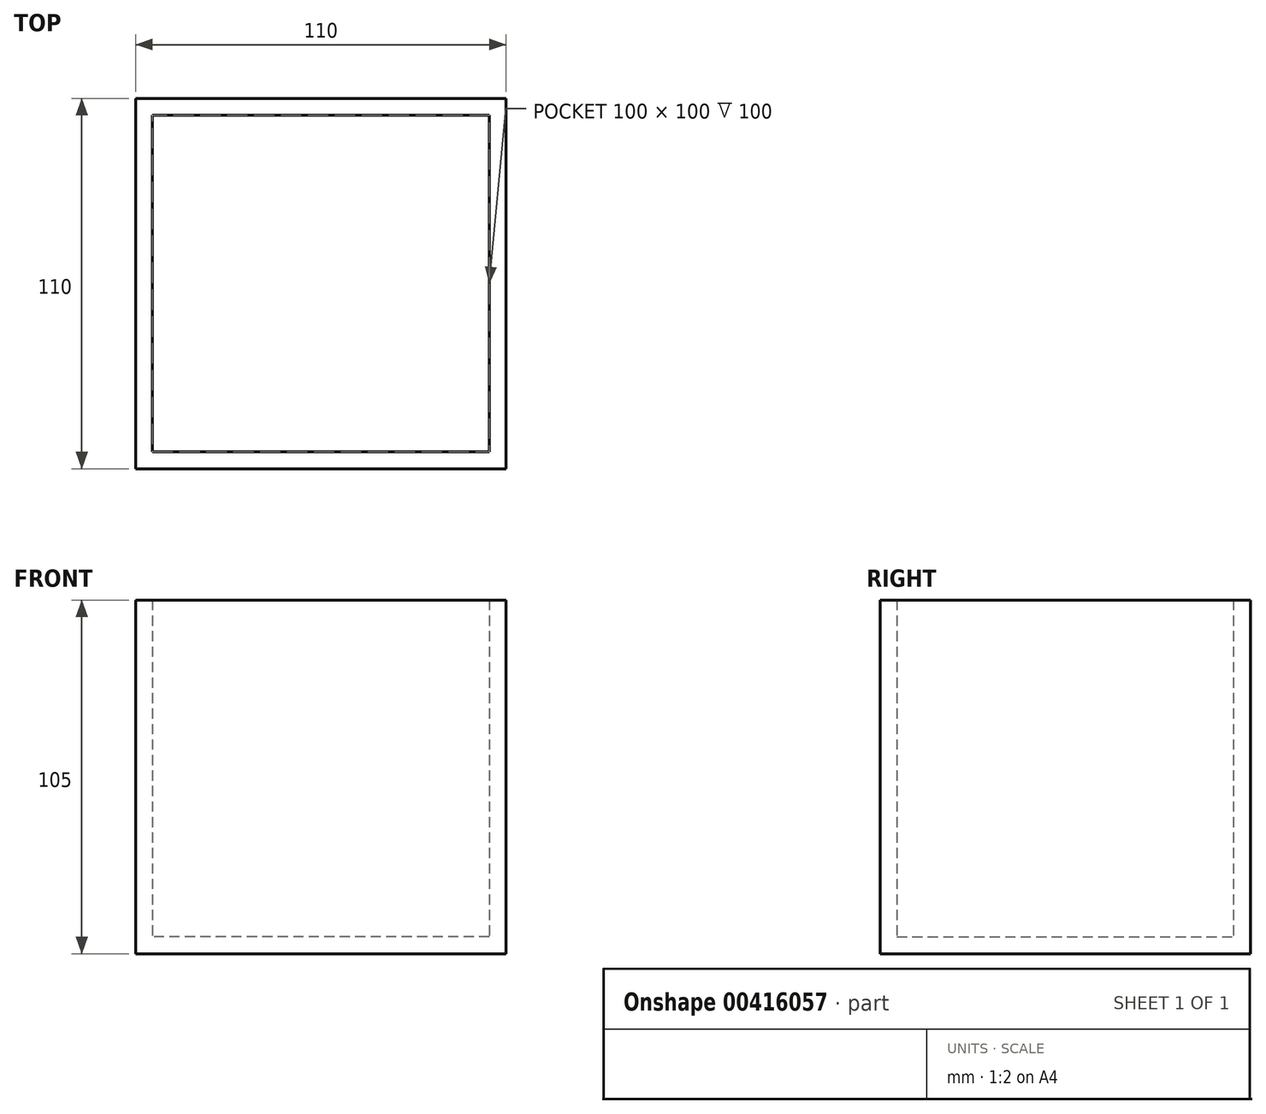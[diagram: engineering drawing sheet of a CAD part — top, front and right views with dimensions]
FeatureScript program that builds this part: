
annotation { "Feature Type Name" : "Feature", "Feature Type Description" : "" }
export const myFeature = defineFeature(function(context is Context, id is Id, definition is map)
    precondition{}
    {
        {
            var Q0;
            Q0=qCreatedBy(makeId("Top.planeOp"),FACE);
            var sketch = newSketch(context, id + "F0", { "sketchPlane" : qUnion([Q0])});
            skLineSegment(sketch, "E0.bottom", {"start": v(50, -50) * mm, "end": v(-50, -50) * mm});
            skLineSegment(sketch, "E0.top", {"start": v(50, 50) * mm, "end": v(-50, 50) * mm});
            skLineSegment(sketch, "E0.left", {"start": v(50, -50) * mm, "end": v(50, 50) * mm});
            skLineSegment(sketch, "E0.right", {"start": v(-50, -50) * mm, "end": v(-50, 50) * mm});
            skPoint(sketch, "E0.middle", {"position": v(0, 0) * mm});
            skSolve(sketch);
        }
        {
            var Q0;
            Q0=makeQuery(id+"F0.imprint","IMPRINT",FACE,{"disambiguationData":[TD([[makeQuery(id+"F0.imprint","IMPRINT",EDGE,{"derivedFrom":sQuery(id+"F0.wireOp",EDGE,"E0.bottom")}),-1.0]])]});
            extrude(context, id + "F1", {"entities" : qUnion([Q0]), "depth" : 100 * mm});
        }
        {
            var Q0;
            Q0=makeQuery(id+"F1.opExtrude","CAP_FACE",FACE,{"disambiguationData":[OSD([sQuery(id+"F0.wireOp",EDGE,"E0.bottom"),sQuery(id+"F0.wireOp",EDGE,"E0.top"),sQuery(id+"F0.wireOp",EDGE,"E0.left"),sQuery(id+"F0.wireOp",EDGE,"E0.right")])],"isStart":false});
            shell(context, id + "F2", {"entities" : qUnion([Q0]), "thickness" : 5 * mm, "oppositeDirection" : true});
        }
    });
